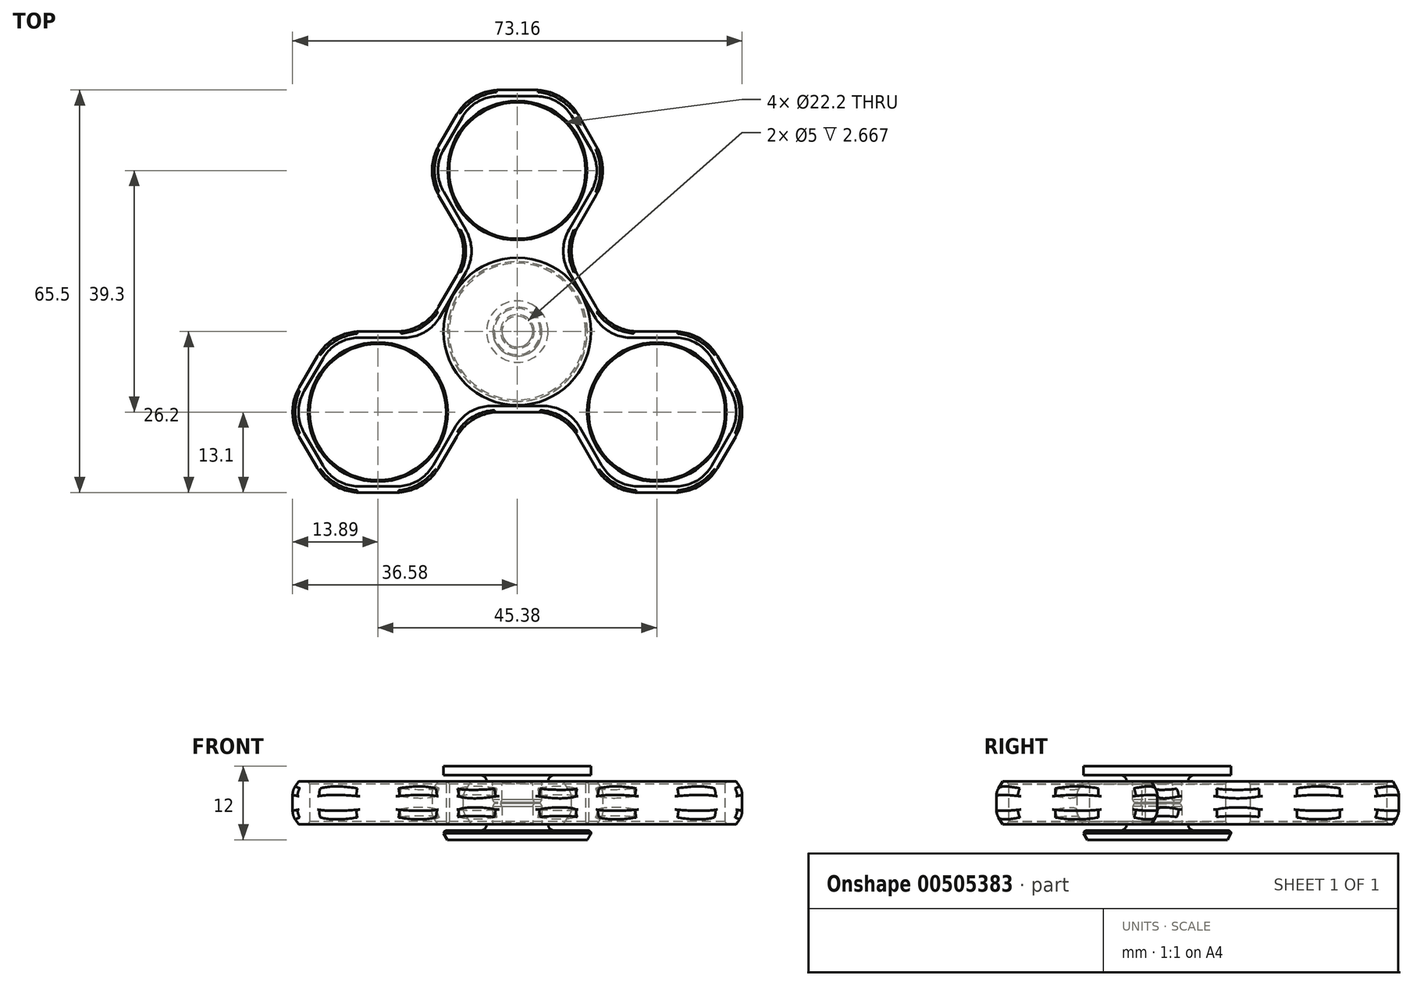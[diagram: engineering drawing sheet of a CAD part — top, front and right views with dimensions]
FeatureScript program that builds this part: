
annotation { "Feature Type Name" : "Feature", "Feature Type Description" : "" }
export const myFeature = defineFeature(function(context is Context, id is Id, definition is map)
    precondition{}
    {
        {
            var Q0;
            Q0=qCreatedBy(makeId("Top.planeOp"),FACE);
            var sketch = newSketch(context, id + "F0", { "sketchPlane" : qUnion([Q0])});
            skCircle(sketch, "E0.cCircle", {"center": v(0, 26.2) * mm, "radius": 13.1 * mm, "construction": true});
            skLineSegment(sketch, "E0.0", {"start": v(7.56, 13.1) * mm, "end": v(-7.56, 13.1) * mm});
            skLineSegment(sketch, "E0.1", {"start": v(-7.56, 13.1) * mm, "end": v(-15.13, 26.2) * mm});
            skLineSegment(sketch, "E0.2", {"start": v(-15.13, 26.2) * mm, "end": v(-7.56, 39.3) * mm});
            skLineSegment(sketch, "E0.3", {"start": v(-7.56, 39.3) * mm, "end": v(7.56, 39.3) * mm});
            skLineSegment(sketch, "E0.4", {"start": v(7.56, 39.3) * mm, "end": v(15.13, 26.2) * mm});
            skLineSegment(sketch, "E0.5", {"start": v(15.13, 26.2) * mm, "end": v(7.56, 13.1) * mm});
            skPoint(sketch, "E0.0.midPoint", {"position": v(0, 13.1) * mm});
            skCircle(sketch, "E1", {"center": v(0, 26.2) * mm, "radius": 11.1 * mm});
            skCircle(sketch, "E2.1.0", {"center": v(-22.69, -13.1) * mm, "radius": 11.1 * mm});
            skLineSegment(sketch, "E2.1.1", {"start": v(-30.25, -26.2) * mm, "end": v(-37.82, -13.1) * mm});
            skLineSegment(sketch, "E2.1.2", {"start": v(-37.82, -13.1) * mm, "end": v(-30.25, 0) * mm});
            skLineSegment(sketch, "E2.1.3", {"start": v(-30.25, 0) * mm, "end": v(-15.13, 0) * mm});
            skLineSegment(sketch, "E2.1.4", {"start": v(-15.13, 0) * mm, "end": v(-7.56, -13.1) * mm});
            skLineSegment(sketch, "E2.1.5", {"start": v(-7.56, -13.1) * mm, "end": v(-15.13, -26.2) * mm});
            skLineSegment(sketch, "E2.1.6", {"start": v(-15.13, -26.2) * mm, "end": v(-30.25, -26.2) * mm});
            skCircle(sketch, "E2.2.0", {"center": v(22.69, -13.1) * mm, "radius": 11.1 * mm});
            skLineSegment(sketch, "E2.2.1", {"start": v(37.82, -13.1) * mm, "end": v(30.25, -26.2) * mm});
            skLineSegment(sketch, "E2.2.2", {"start": v(30.25, -26.2) * mm, "end": v(15.13, -26.2) * mm});
            skLineSegment(sketch, "E2.2.3", {"start": v(15.13, -26.2) * mm, "end": v(7.56, -13.1) * mm});
            skLineSegment(sketch, "E2.2.4", {"start": v(7.56, -13.1) * mm, "end": v(15.13, 0) * mm});
            skLineSegment(sketch, "E2.2.5", {"start": v(15.13, 0) * mm, "end": v(30.25, 0) * mm});
            skLineSegment(sketch, "E2.2.6", {"start": v(30.25, 0) * mm, "end": v(37.82, -13.1) * mm});
            skPoint(sketch, "E2.center", {"position": v(0, 0) * mm});
            skCircle(sketch, "E3", {"center": v(0, 0) * mm, "radius": 11.1 * mm});
            skLineSegment(sketch, "E4", {"start": v(7.56, 13.1) * mm, "end": v(15.13, 0) * mm});
            skLineSegment(sketch, "E5", {"start": v(7.56, -13.1) * mm, "end": v(-7.56, -13.1) * mm});
            skLineSegment(sketch, "E6", {"start": v(-15.13, 0) * mm, "end": v(-7.56, 13.1) * mm});
            skCircle(sketch, "E7", {"center": v(0, 0) * mm, "radius": 40.02 * mm, "construction": true});
            skSolve(sketch);
        }
        {
            var Q0;
            Q0=makeQuery(id+"F0.imprint","IMPRINT",FACE,{"disambiguationData":[TD([[makeQuery(id+"F0.imprint","IMPRINT",EDGE,{"derivedFrom":sQuery(id+"F0.wireOp",EDGE,"E0.0")}),-1.0]])]});
            var Q1;
            Q1=makeQuery(id+"F0.imprint","IMPRINT",FACE,{"disambiguationData":[TD([[makeQuery(id+"F0.imprint","IMPRINT",EDGE,{"derivedFrom":sQuery(id+"F0.wireOp",EDGE,"E0.0")}),1.0]])]});
            var Q2;
            Q2=makeQuery(id+"F0.imprint","IMPRINT",FACE,{"disambiguationData":[TD([[makeQuery(id+"F0.imprint","IMPRINT",EDGE,{"derivedFrom":sQuery(id+"F0.wireOp",EDGE,"E2.1.0")}),-1.0]])]});
            var Q3;
            Q3=makeQuery(id+"F0.imprint","IMPRINT",FACE,{"disambiguationData":[TD([[makeQuery(id+"F0.imprint","IMPRINT",EDGE,{"derivedFrom":sQuery(id+"F0.wireOp",EDGE,"E2.2.0")}),-1.0]])]});
            extrude(context, id + "F1", {"entities" : qUnion([Q0, Q1, Q2, Q3]), "depth" : 7 * mm});
        }
        {
            var Q0;
            Q0=makeQuery(id+"F1.opExtrude","CAP_EDGE",EDGE,{"disambiguationData":[OSD([sQuery(id+"F0.wireOp",EDGE,"E0.3")])],"isStart":false});
            var Q1;
            Q1=makeQuery(id+"F1.opExtrude","CAP_EDGE",EDGE,{"disambiguationData":[OSD([sQuery(id+"F0.wireOp",EDGE,"E0.2")])],"isStart":false});
            var Q2;
            Q2=makeQuery(id+"F1.opExtrude","CAP_EDGE",EDGE,{"disambiguationData":[OSD([sQuery(id+"F0.wireOp",EDGE,"E0.1")])],"isStart":false});
            var Q3;
            Q3=makeQuery(id+"F1.opExtrude","CAP_EDGE",EDGE,{"disambiguationData":[OSD([sQuery(id+"F0.wireOp",EDGE,"E0.4")])],"isStart":false});
            var Q4;
            Q4=makeQuery(id+"F1.opExtrude","CAP_EDGE",EDGE,{"disambiguationData":[OSD([sQuery(id+"F0.wireOp",EDGE,"E0.5")])],"isStart":false});
            var Q5;
            Q5=makeQuery(id+"F1.opExtrude","CAP_EDGE",EDGE,{"disambiguationData":[OSD([sQuery(id+"F0.wireOp",EDGE,"E6")])],"isStart":false});
            var Q6;
            Q6=makeQuery(id+"F1.opExtrude","CAP_EDGE",EDGE,{"disambiguationData":[OSD([sQuery(id+"F0.wireOp",EDGE,"E4")])],"isStart":false});
            var Q7;
            Q7=makeQuery(id+"F1.opExtrude","CAP_EDGE",EDGE,{"disambiguationData":[OSD([sQuery(id+"F0.wireOp",EDGE,"E2.2.5")])],"isStart":false});
            var Q8;
            Q8=makeQuery(id+"F1.opExtrude","CAP_EDGE",EDGE,{"disambiguationData":[OSD([sQuery(id+"F0.wireOp",EDGE,"E2.2.6")])],"isStart":false});
            var Q9;
            Q9=makeQuery(id+"F1.opExtrude","CAP_EDGE",EDGE,{"disambiguationData":[OSD([sQuery(id+"F0.wireOp",EDGE,"E2.2.1")])],"isStart":false});
            var Q10;
            Q10=makeQuery(id+"F1.opExtrude","CAP_EDGE",EDGE,{"disambiguationData":[OSD([sQuery(id+"F0.wireOp",EDGE,"E2.2.2")])],"isStart":false});
            var Q11;
            Q11=makeQuery(id+"F1.opExtrude","CAP_EDGE",EDGE,{"disambiguationData":[OSD([sQuery(id+"F0.wireOp",EDGE,"E2.2.3")])],"isStart":false});
            var Q12;
            Q12=makeQuery(id+"F1.opExtrude","CAP_EDGE",EDGE,{"disambiguationData":[OSD([sQuery(id+"F0.wireOp",EDGE,"E5")])],"isStart":false});
            var Q13;
            Q13=makeQuery(id+"F1.opExtrude","CAP_EDGE",EDGE,{"disambiguationData":[OSD([sQuery(id+"F0.wireOp",EDGE,"E2.1.5")])],"isStart":false});
            var Q14;
            Q14=makeQuery(id+"F1.opExtrude","CAP_EDGE",EDGE,{"disambiguationData":[OSD([sQuery(id+"F0.wireOp",EDGE,"E2.1.6")])],"isStart":false});
            var Q15;
            Q15=makeQuery(id+"F1.opExtrude","CAP_EDGE",EDGE,{"disambiguationData":[OSD([sQuery(id+"F0.wireOp",EDGE,"E2.1.1")])],"isStart":false});
            var Q16;
            Q16=makeQuery(id+"F1.opExtrude","CAP_EDGE",EDGE,{"disambiguationData":[OSD([sQuery(id+"F0.wireOp",EDGE,"E2.1.2")])],"isStart":false});
            var Q17;
            Q17=makeQuery(id+"F1.opExtrude","CAP_EDGE",EDGE,{"disambiguationData":[OSD([sQuery(id+"F0.wireOp",EDGE,"E2.1.3")])],"isStart":false});
            chamfer(context, id + "F2", {"entities" : qUnion([Q0, Q1, Q2, Q3, Q4, Q5, Q6, Q7, Q8, Q9, Q10, Q11, Q12, Q13, Q14, Q15, Q16, Q17]), "chamferType" : ChamferType.OFFSET_ANGLE, "width" : 1 * mm, "oppositeDirection" : true, "angle" : 60 * degree, "tangentPropagation" : true});
        }
        {
            var Q0;
            Q0=makeQuery(id+"F1.opExtrude","CAP_EDGE",EDGE,{"disambiguationData":[OSD([sQuery(id+"F0.wireOp",EDGE,"E2.1.3")])],"isStart":true});
            var Q1;
            Q1=makeQuery(id+"F1.opExtrude","CAP_EDGE",EDGE,{"disambiguationData":[OSD([sQuery(id+"F0.wireOp",EDGE,"E2.1.2")])],"isStart":true});
            var Q2;
            Q2=makeQuery(id+"F1.opExtrude","CAP_EDGE",EDGE,{"disambiguationData":[OSD([sQuery(id+"F0.wireOp",EDGE,"E2.1.1")])],"isStart":true});
            var Q3;
            Q3=makeQuery(id+"F1.opExtrude","CAP_EDGE",EDGE,{"disambiguationData":[OSD([sQuery(id+"F0.wireOp",EDGE,"E2.1.6")])],"isStart":true});
            var Q4;
            Q4=makeQuery(id+"F1.opExtrude","CAP_EDGE",EDGE,{"disambiguationData":[OSD([sQuery(id+"F0.wireOp",EDGE,"E2.1.5")])],"isStart":true});
            var Q5;
            Q5=makeQuery(id+"F1.opExtrude","CAP_EDGE",EDGE,{"disambiguationData":[OSD([sQuery(id+"F0.wireOp",EDGE,"E5")])],"isStart":true});
            var Q6;
            Q6=makeQuery(id+"F1.opExtrude","CAP_EDGE",EDGE,{"disambiguationData":[OSD([sQuery(id+"F0.wireOp",EDGE,"E2.2.3")])],"isStart":true});
            var Q7;
            Q7=makeQuery(id+"F1.opExtrude","CAP_EDGE",EDGE,{"disambiguationData":[OSD([sQuery(id+"F0.wireOp",EDGE,"E2.2.2")])],"isStart":true});
            var Q8;
            Q8=makeQuery(id+"F1.opExtrude","CAP_EDGE",EDGE,{"disambiguationData":[OSD([sQuery(id+"F0.wireOp",EDGE,"E2.2.1")])],"isStart":true});
            var Q9;
            Q9=makeQuery(id+"F1.opExtrude","CAP_EDGE",EDGE,{"disambiguationData":[OSD([sQuery(id+"F0.wireOp",EDGE,"E2.2.6")])],"isStart":true});
            var Q10;
            Q10=makeQuery(id+"F1.opExtrude","CAP_EDGE",EDGE,{"disambiguationData":[OSD([sQuery(id+"F0.wireOp",EDGE,"E2.2.5")])],"isStart":true});
            var Q11;
            Q11=makeQuery(id+"F1.opExtrude","CAP_EDGE",EDGE,{"disambiguationData":[OSD([sQuery(id+"F0.wireOp",EDGE,"E4")])],"isStart":true});
            var Q12;
            Q12=makeQuery(id+"F1.opExtrude","CAP_EDGE",EDGE,{"disambiguationData":[OSD([sQuery(id+"F0.wireOp",EDGE,"E0.5")])],"isStart":true});
            var Q13;
            Q13=makeQuery(id+"F1.opExtrude","CAP_EDGE",EDGE,{"disambiguationData":[OSD([sQuery(id+"F0.wireOp",EDGE,"E6")])],"isStart":true});
            var Q14;
            Q14=makeQuery(id+"F1.opExtrude","CAP_EDGE",EDGE,{"disambiguationData":[OSD([sQuery(id+"F0.wireOp",EDGE,"E0.1")])],"isStart":true});
            var Q15;
            Q15=makeQuery(id+"F1.opExtrude","CAP_EDGE",EDGE,{"disambiguationData":[OSD([sQuery(id+"F0.wireOp",EDGE,"E0.2")])],"isStart":true});
            var Q16;
            Q16=makeQuery(id+"F1.opExtrude","CAP_EDGE",EDGE,{"disambiguationData":[OSD([sQuery(id+"F0.wireOp",EDGE,"E0.3")])],"isStart":true});
            var Q17;
            Q17=makeQuery(id+"F1.opExtrude","CAP_EDGE",EDGE,{"disambiguationData":[OSD([sQuery(id+"F0.wireOp",EDGE,"E0.4")])],"isStart":true});
            chamfer(context, id + "F3", {"entities" : qUnion([Q0, Q1, Q2, Q3, Q4, Q5, Q6, Q7, Q8, Q9, Q10, Q11, Q12, Q13, Q14, Q15, Q16, Q17]), "chamferType" : ChamferType.OFFSET_ANGLE, "width" : 1 * mm, "oppositeDirection" : false, "angle" : 60 * degree, "tangentPropagation" : true});
        }
        {
            var Q0;
            Q0=makeQuery(id+"F1.opExtrude","SWEPT_EDGE",EDGE,{"disambiguationData":[OSD([sQuery(id+"F0.wireOp",EDGE,"E0.1"),sQuery(id+"F0.wireOp",EDGE,"E0.2")])]});
            var Q1;
            Q1=makeQuery(id+"F3.opChamfer","BLEND_EDGE",EDGE,{"blendedFrom":[makeQuery(id+"F1.opExtrude","CAP_EDGE",EDGE,{"disambiguationData":[OSD([sQuery(id+"F0.wireOp",EDGE,"E0.1")])],"isStart":true}),makeQuery(id+"F1.opExtrude","CAP_EDGE",EDGE,{"disambiguationData":[OSD([sQuery(id+"F0.wireOp",EDGE,"E0.2")])],"isStart":true})],"blendedInto":[]});
            var Q2;
            Q2=makeQuery(id+"F2.opChamfer","BLEND_EDGE",EDGE,{"blendedFrom":[makeQuery(id+"F1.opExtrude","CAP_EDGE",EDGE,{"disambiguationData":[OSD([sQuery(id+"F0.wireOp",EDGE,"E0.1")])],"isStart":false}),makeQuery(id+"F1.opExtrude","CAP_EDGE",EDGE,{"disambiguationData":[OSD([sQuery(id+"F0.wireOp",EDGE,"E0.2")])],"isStart":false})],"blendedInto":[]});
            var Q3;
            Q3=makeQuery(id+"F1.opExtrude","SWEPT_EDGE",EDGE,{"disambiguationData":[OSD([sQuery(id+"F0.wireOp",EDGE,"E0.2"),sQuery(id+"F0.wireOp",EDGE,"E0.3")])]});
            var Q4;
            Q4=makeQuery(id+"F3.opChamfer","BLEND_EDGE",EDGE,{"blendedFrom":[makeQuery(id+"F1.opExtrude","CAP_EDGE",EDGE,{"disambiguationData":[OSD([sQuery(id+"F0.wireOp",EDGE,"E0.2")])],"isStart":true}),makeQuery(id+"F1.opExtrude","CAP_EDGE",EDGE,{"disambiguationData":[OSD([sQuery(id+"F0.wireOp",EDGE,"E0.3")])],"isStart":true})],"blendedInto":[]});
            var Q5;
            Q5=makeQuery(id+"F2.opChamfer","BLEND_EDGE",EDGE,{"blendedFrom":[makeQuery(id+"F1.opExtrude","CAP_EDGE",EDGE,{"disambiguationData":[OSD([sQuery(id+"F0.wireOp",EDGE,"E0.2")])],"isStart":false}),makeQuery(id+"F1.opExtrude","CAP_EDGE",EDGE,{"disambiguationData":[OSD([sQuery(id+"F0.wireOp",EDGE,"E0.3")])],"isStart":false})],"blendedInto":[]});
            var Q6;
            Q6=makeQuery(id+"F3.opChamfer","BLEND_EDGE",EDGE,{"blendedFrom":[makeQuery(id+"F1.opExtrude","CAP_EDGE",EDGE,{"disambiguationData":[OSD([sQuery(id+"F0.wireOp",EDGE,"E0.3")])],"isStart":true}),makeQuery(id+"F1.opExtrude","CAP_EDGE",EDGE,{"disambiguationData":[OSD([sQuery(id+"F0.wireOp",EDGE,"E0.4")])],"isStart":true})],"blendedInto":[]});
            var Q7;
            Q7=makeQuery(id+"F1.opExtrude","SWEPT_EDGE",EDGE,{"disambiguationData":[OSD([sQuery(id+"F0.wireOp",EDGE,"E0.3"),sQuery(id+"F0.wireOp",EDGE,"E0.4")])]});
            var Q8;
            Q8=makeQuery(id+"F2.opChamfer","BLEND_EDGE",EDGE,{"blendedFrom":[makeQuery(id+"F1.opExtrude","CAP_EDGE",EDGE,{"disambiguationData":[OSD([sQuery(id+"F0.wireOp",EDGE,"E0.3")])],"isStart":false}),makeQuery(id+"F1.opExtrude","CAP_EDGE",EDGE,{"disambiguationData":[OSD([sQuery(id+"F0.wireOp",EDGE,"E0.4")])],"isStart":false})],"blendedInto":[]});
            var Q9;
            Q9=makeQuery(id+"F3.opChamfer","BLEND_EDGE",EDGE,{"blendedFrom":[makeQuery(id+"F1.opExtrude","CAP_EDGE",EDGE,{"disambiguationData":[OSD([sQuery(id+"F0.wireOp",EDGE,"E0.4")])],"isStart":true}),makeQuery(id+"F1.opExtrude","CAP_EDGE",EDGE,{"disambiguationData":[OSD([sQuery(id+"F0.wireOp",EDGE,"E0.5")])],"isStart":true})],"blendedInto":[]});
            var Q10;
            Q10=makeQuery(id+"F1.opExtrude","SWEPT_EDGE",EDGE,{"disambiguationData":[OSD([sQuery(id+"F0.wireOp",EDGE,"E0.4"),sQuery(id+"F0.wireOp",EDGE,"E0.5")])]});
            var Q11;
            Q11=makeQuery(id+"F2.opChamfer","BLEND_EDGE",EDGE,{"blendedFrom":[makeQuery(id+"F1.opExtrude","CAP_EDGE",EDGE,{"disambiguationData":[OSD([sQuery(id+"F0.wireOp",EDGE,"E0.4")])],"isStart":false}),makeQuery(id+"F1.opExtrude","CAP_EDGE",EDGE,{"disambiguationData":[OSD([sQuery(id+"F0.wireOp",EDGE,"E0.5")])],"isStart":false})],"blendedInto":[]});
            var Q12;
            Q12=makeQuery(id+"F3.opChamfer","BLEND_EDGE",EDGE,{"blendedFrom":[makeQuery(id+"F1.opExtrude","CAP_EDGE",EDGE,{"disambiguationData":[OSD([sQuery(id+"F0.wireOp",EDGE,"E0.5")])],"isStart":true}),makeQuery(id+"F1.opExtrude","CAP_EDGE",EDGE,{"disambiguationData":[OSD([sQuery(id+"F0.wireOp",EDGE,"E4")])],"isStart":true})],"blendedInto":[]});
            var Q13;
            Q13=makeQuery(id+"F1.opExtrude","SWEPT_EDGE",EDGE,{"disambiguationData":[OSD([sQuery(id+"F0.wireOp",EDGE,"E0.0"),sQuery(id+"F0.wireOp",EDGE,"E0.5"),sQuery(id+"F0.wireOp",EDGE,"E4")])]});
            var Q14;
            Q14=makeQuery(id+"F2.opChamfer","BLEND_EDGE",EDGE,{"blendedFrom":[makeQuery(id+"F1.opExtrude","CAP_EDGE",EDGE,{"disambiguationData":[OSD([sQuery(id+"F0.wireOp",EDGE,"E0.5")])],"isStart":false}),makeQuery(id+"F1.opExtrude","CAP_EDGE",EDGE,{"disambiguationData":[OSD([sQuery(id+"F0.wireOp",EDGE,"E4")])],"isStart":false})],"blendedInto":[]});
            var Q15;
            Q15=makeQuery(id+"F3.opChamfer","BLEND_EDGE",EDGE,{"blendedFrom":[makeQuery(id+"F1.opExtrude","CAP_EDGE",EDGE,{"disambiguationData":[OSD([sQuery(id+"F0.wireOp",EDGE,"E2.2.5")])],"isStart":true}),makeQuery(id+"F1.opExtrude","CAP_EDGE",EDGE,{"disambiguationData":[OSD([sQuery(id+"F0.wireOp",EDGE,"E4")])],"isStart":true})],"blendedInto":[]});
            var Q16;
            Q16=makeQuery(id+"F1.opExtrude","SWEPT_EDGE",EDGE,{"disambiguationData":[OSD([sQuery(id+"F0.wireOp",EDGE,"E2.2.4"),sQuery(id+"F0.wireOp",EDGE,"E2.2.5"),sQuery(id+"F0.wireOp",EDGE,"E4")])]});
            var Q17;
            Q17=makeQuery(id+"F2.opChamfer","BLEND_EDGE",EDGE,{"blendedFrom":[makeQuery(id+"F1.opExtrude","CAP_EDGE",EDGE,{"disambiguationData":[OSD([sQuery(id+"F0.wireOp",EDGE,"E2.2.5")])],"isStart":false}),makeQuery(id+"F1.opExtrude","CAP_EDGE",EDGE,{"disambiguationData":[OSD([sQuery(id+"F0.wireOp",EDGE,"E4")])],"isStart":false})],"blendedInto":[]});
            var Q18;
            Q18=makeQuery(id+"F2.opChamfer","BLEND_EDGE",EDGE,{"blendedFrom":[makeQuery(id+"F1.opExtrude","CAP_EDGE",EDGE,{"disambiguationData":[OSD([sQuery(id+"F0.wireOp",EDGE,"E2.2.5")])],"isStart":false}),makeQuery(id+"F1.opExtrude","CAP_EDGE",EDGE,{"disambiguationData":[OSD([sQuery(id+"F0.wireOp",EDGE,"E2.2.6")])],"isStart":false})],"blendedInto":[]});
            var Q19;
            Q19=makeQuery(id+"F1.opExtrude","SWEPT_EDGE",EDGE,{"disambiguationData":[OSD([sQuery(id+"F0.wireOp",EDGE,"E2.2.5"),sQuery(id+"F0.wireOp",EDGE,"E2.2.6")])]});
            var Q20;
            Q20=makeQuery(id+"F3.opChamfer","BLEND_EDGE",EDGE,{"blendedFrom":[makeQuery(id+"F1.opExtrude","CAP_EDGE",EDGE,{"disambiguationData":[OSD([sQuery(id+"F0.wireOp",EDGE,"E2.2.5")])],"isStart":true}),makeQuery(id+"F1.opExtrude","CAP_EDGE",EDGE,{"disambiguationData":[OSD([sQuery(id+"F0.wireOp",EDGE,"E2.2.6")])],"isStart":true})],"blendedInto":[]});
            var Q21;
            Q21=makeQuery(id+"F3.opChamfer","BLEND_EDGE",EDGE,{"blendedFrom":[makeQuery(id+"F1.opExtrude","CAP_EDGE",EDGE,{"disambiguationData":[OSD([sQuery(id+"F0.wireOp",EDGE,"E2.2.1")])],"isStart":true}),makeQuery(id+"F1.opExtrude","CAP_EDGE",EDGE,{"disambiguationData":[OSD([sQuery(id+"F0.wireOp",EDGE,"E2.2.6")])],"isStart":true})],"blendedInto":[]});
            var Q22;
            Q22=makeQuery(id+"F1.opExtrude","SWEPT_EDGE",EDGE,{"disambiguationData":[OSD([sQuery(id+"F0.wireOp",EDGE,"E2.2.1"),sQuery(id+"F0.wireOp",EDGE,"E2.2.6")])]});
            var Q23;
            Q23=makeQuery(id+"F2.opChamfer","BLEND_EDGE",EDGE,{"blendedFrom":[makeQuery(id+"F1.opExtrude","CAP_EDGE",EDGE,{"disambiguationData":[OSD([sQuery(id+"F0.wireOp",EDGE,"E2.2.1")])],"isStart":false}),makeQuery(id+"F1.opExtrude","CAP_EDGE",EDGE,{"disambiguationData":[OSD([sQuery(id+"F0.wireOp",EDGE,"E2.2.6")])],"isStart":false})],"blendedInto":[]});
            var Q24;
            Q24=makeQuery(id+"F3.opChamfer","BLEND_EDGE",EDGE,{"blendedFrom":[makeQuery(id+"F1.opExtrude","CAP_EDGE",EDGE,{"disambiguationData":[OSD([sQuery(id+"F0.wireOp",EDGE,"E2.2.1")])],"isStart":true}),makeQuery(id+"F1.opExtrude","CAP_EDGE",EDGE,{"disambiguationData":[OSD([sQuery(id+"F0.wireOp",EDGE,"E2.2.2")])],"isStart":true})],"blendedInto":[]});
            var Q25;
            Q25=makeQuery(id+"F1.opExtrude","SWEPT_EDGE",EDGE,{"disambiguationData":[OSD([sQuery(id+"F0.wireOp",EDGE,"E2.2.1"),sQuery(id+"F0.wireOp",EDGE,"E2.2.2")])]});
            var Q26;
            Q26=makeQuery(id+"F2.opChamfer","BLEND_EDGE",EDGE,{"blendedFrom":[makeQuery(id+"F1.opExtrude","CAP_EDGE",EDGE,{"disambiguationData":[OSD([sQuery(id+"F0.wireOp",EDGE,"E2.2.1")])],"isStart":false}),makeQuery(id+"F1.opExtrude","CAP_EDGE",EDGE,{"disambiguationData":[OSD([sQuery(id+"F0.wireOp",EDGE,"E2.2.2")])],"isStart":false})],"blendedInto":[]});
            var Q27;
            Q27=makeQuery(id+"F3.opChamfer","BLEND_EDGE",EDGE,{"blendedFrom":[makeQuery(id+"F1.opExtrude","CAP_EDGE",EDGE,{"disambiguationData":[OSD([sQuery(id+"F0.wireOp",EDGE,"E2.2.2")])],"isStart":true}),makeQuery(id+"F1.opExtrude","CAP_EDGE",EDGE,{"disambiguationData":[OSD([sQuery(id+"F0.wireOp",EDGE,"E2.2.3")])],"isStart":true})],"blendedInto":[]});
            var Q28;
            Q28=makeQuery(id+"F1.opExtrude","SWEPT_EDGE",EDGE,{"disambiguationData":[OSD([sQuery(id+"F0.wireOp",EDGE,"E2.2.2"),sQuery(id+"F0.wireOp",EDGE,"E2.2.3")])]});
            var Q29;
            Q29=makeQuery(id+"F2.opChamfer","BLEND_EDGE",EDGE,{"blendedFrom":[makeQuery(id+"F1.opExtrude","CAP_EDGE",EDGE,{"disambiguationData":[OSD([sQuery(id+"F0.wireOp",EDGE,"E2.2.2")])],"isStart":false}),makeQuery(id+"F1.opExtrude","CAP_EDGE",EDGE,{"disambiguationData":[OSD([sQuery(id+"F0.wireOp",EDGE,"E2.2.3")])],"isStart":false})],"blendedInto":[]});
            var Q30;
            Q30=makeQuery(id+"F3.opChamfer","BLEND_EDGE",EDGE,{"blendedFrom":[makeQuery(id+"F1.opExtrude","CAP_EDGE",EDGE,{"disambiguationData":[OSD([sQuery(id+"F0.wireOp",EDGE,"E2.2.3")])],"isStart":true}),makeQuery(id+"F1.opExtrude","CAP_EDGE",EDGE,{"disambiguationData":[OSD([sQuery(id+"F0.wireOp",EDGE,"E5")])],"isStart":true})],"blendedInto":[]});
            var Q31;
            Q31=makeQuery(id+"F1.opExtrude","SWEPT_EDGE",EDGE,{"disambiguationData":[OSD([sQuery(id+"F0.wireOp",EDGE,"E2.2.3"),sQuery(id+"F0.wireOp",EDGE,"E2.2.4"),sQuery(id+"F0.wireOp",EDGE,"E5")])]});
            var Q32;
            Q32=makeQuery(id+"F2.opChamfer","BLEND_EDGE",EDGE,{"blendedFrom":[makeQuery(id+"F1.opExtrude","CAP_EDGE",EDGE,{"disambiguationData":[OSD([sQuery(id+"F0.wireOp",EDGE,"E2.2.3")])],"isStart":false}),makeQuery(id+"F1.opExtrude","CAP_EDGE",EDGE,{"disambiguationData":[OSD([sQuery(id+"F0.wireOp",EDGE,"E5")])],"isStart":false})],"blendedInto":[]});
            var Q33;
            Q33=makeQuery(id+"F3.opChamfer","BLEND_EDGE",EDGE,{"blendedFrom":[makeQuery(id+"F1.opExtrude","CAP_EDGE",EDGE,{"disambiguationData":[OSD([sQuery(id+"F0.wireOp",EDGE,"E2.1.5")])],"isStart":true}),makeQuery(id+"F1.opExtrude","CAP_EDGE",EDGE,{"disambiguationData":[OSD([sQuery(id+"F0.wireOp",EDGE,"E5")])],"isStart":true})],"blendedInto":[]});
            var Q34;
            Q34=makeQuery(id+"F1.opExtrude","SWEPT_EDGE",EDGE,{"disambiguationData":[OSD([sQuery(id+"F0.wireOp",EDGE,"E2.1.4"),sQuery(id+"F0.wireOp",EDGE,"E2.1.5"),sQuery(id+"F0.wireOp",EDGE,"E5")])]});
            var Q35;
            Q35=makeQuery(id+"F2.opChamfer","BLEND_EDGE",EDGE,{"blendedFrom":[makeQuery(id+"F1.opExtrude","CAP_EDGE",EDGE,{"disambiguationData":[OSD([sQuery(id+"F0.wireOp",EDGE,"E2.1.5")])],"isStart":false}),makeQuery(id+"F1.opExtrude","CAP_EDGE",EDGE,{"disambiguationData":[OSD([sQuery(id+"F0.wireOp",EDGE,"E5")])],"isStart":false})],"blendedInto":[]});
            var Q36;
            Q36=makeQuery(id+"F3.opChamfer","BLEND_EDGE",EDGE,{"blendedFrom":[makeQuery(id+"F1.opExtrude","CAP_EDGE",EDGE,{"disambiguationData":[OSD([sQuery(id+"F0.wireOp",EDGE,"E2.1.5")])],"isStart":true}),makeQuery(id+"F1.opExtrude","CAP_EDGE",EDGE,{"disambiguationData":[OSD([sQuery(id+"F0.wireOp",EDGE,"E2.1.6")])],"isStart":true})],"blendedInto":[]});
            var Q37;
            Q37=makeQuery(id+"F1.opExtrude","SWEPT_EDGE",EDGE,{"disambiguationData":[OSD([sQuery(id+"F0.wireOp",EDGE,"E2.1.5"),sQuery(id+"F0.wireOp",EDGE,"E2.1.6")])]});
            var Q38;
            Q38=makeQuery(id+"F2.opChamfer","BLEND_EDGE",EDGE,{"blendedFrom":[makeQuery(id+"F1.opExtrude","CAP_EDGE",EDGE,{"disambiguationData":[OSD([sQuery(id+"F0.wireOp",EDGE,"E2.1.5")])],"isStart":false}),makeQuery(id+"F1.opExtrude","CAP_EDGE",EDGE,{"disambiguationData":[OSD([sQuery(id+"F0.wireOp",EDGE,"E2.1.6")])],"isStart":false})],"blendedInto":[]});
            var Q39;
            Q39=makeQuery(id+"F3.opChamfer","BLEND_EDGE",EDGE,{"blendedFrom":[makeQuery(id+"F1.opExtrude","CAP_EDGE",EDGE,{"disambiguationData":[OSD([sQuery(id+"F0.wireOp",EDGE,"E2.1.1")])],"isStart":true}),makeQuery(id+"F1.opExtrude","CAP_EDGE",EDGE,{"disambiguationData":[OSD([sQuery(id+"F0.wireOp",EDGE,"E2.1.6")])],"isStart":true})],"blendedInto":[]});
            var Q40;
            Q40=makeQuery(id+"F1.opExtrude","SWEPT_EDGE",EDGE,{"disambiguationData":[OSD([sQuery(id+"F0.wireOp",EDGE,"E2.1.1"),sQuery(id+"F0.wireOp",EDGE,"E2.1.6")])]});
            var Q41;
            Q41=makeQuery(id+"F2.opChamfer","BLEND_EDGE",EDGE,{"blendedFrom":[makeQuery(id+"F1.opExtrude","CAP_EDGE",EDGE,{"disambiguationData":[OSD([sQuery(id+"F0.wireOp",EDGE,"E2.1.1")])],"isStart":false}),makeQuery(id+"F1.opExtrude","CAP_EDGE",EDGE,{"disambiguationData":[OSD([sQuery(id+"F0.wireOp",EDGE,"E2.1.6")])],"isStart":false})],"blendedInto":[]});
            var Q42;
            Q42=makeQuery(id+"F3.opChamfer","BLEND_EDGE",EDGE,{"blendedFrom":[makeQuery(id+"F1.opExtrude","CAP_EDGE",EDGE,{"disambiguationData":[OSD([sQuery(id+"F0.wireOp",EDGE,"E2.1.1")])],"isStart":true}),makeQuery(id+"F1.opExtrude","CAP_EDGE",EDGE,{"disambiguationData":[OSD([sQuery(id+"F0.wireOp",EDGE,"E2.1.2")])],"isStart":true})],"blendedInto":[]});
            var Q43;
            Q43=makeQuery(id+"F1.opExtrude","SWEPT_EDGE",EDGE,{"disambiguationData":[OSD([sQuery(id+"F0.wireOp",EDGE,"E2.1.1"),sQuery(id+"F0.wireOp",EDGE,"E2.1.2")])]});
            var Q44;
            Q44=makeQuery(id+"F2.opChamfer","BLEND_EDGE",EDGE,{"blendedFrom":[makeQuery(id+"F1.opExtrude","CAP_EDGE",EDGE,{"disambiguationData":[OSD([sQuery(id+"F0.wireOp",EDGE,"E2.1.1")])],"isStart":false}),makeQuery(id+"F1.opExtrude","CAP_EDGE",EDGE,{"disambiguationData":[OSD([sQuery(id+"F0.wireOp",EDGE,"E2.1.2")])],"isStart":false})],"blendedInto":[]});
            var Q45;
            Q45=makeQuery(id+"F3.opChamfer","BLEND_EDGE",EDGE,{"blendedFrom":[makeQuery(id+"F1.opExtrude","CAP_EDGE",EDGE,{"disambiguationData":[OSD([sQuery(id+"F0.wireOp",EDGE,"E2.1.2")])],"isStart":true}),makeQuery(id+"F1.opExtrude","CAP_EDGE",EDGE,{"disambiguationData":[OSD([sQuery(id+"F0.wireOp",EDGE,"E2.1.3")])],"isStart":true})],"blendedInto":[]});
            var Q46;
            Q46=makeQuery(id+"F1.opExtrude","SWEPT_EDGE",EDGE,{"disambiguationData":[OSD([sQuery(id+"F0.wireOp",EDGE,"E2.1.2"),sQuery(id+"F0.wireOp",EDGE,"E2.1.3")])]});
            var Q47;
            Q47=makeQuery(id+"F2.opChamfer","BLEND_EDGE",EDGE,{"blendedFrom":[makeQuery(id+"F1.opExtrude","CAP_EDGE",EDGE,{"disambiguationData":[OSD([sQuery(id+"F0.wireOp",EDGE,"E2.1.2")])],"isStart":false}),makeQuery(id+"F1.opExtrude","CAP_EDGE",EDGE,{"disambiguationData":[OSD([sQuery(id+"F0.wireOp",EDGE,"E2.1.3")])],"isStart":false})],"blendedInto":[]});
            var Q48;
            Q48=makeQuery(id+"F3.opChamfer","BLEND_EDGE",EDGE,{"blendedFrom":[makeQuery(id+"F1.opExtrude","CAP_EDGE",EDGE,{"disambiguationData":[OSD([sQuery(id+"F0.wireOp",EDGE,"E2.1.3")])],"isStart":true}),makeQuery(id+"F1.opExtrude","CAP_EDGE",EDGE,{"disambiguationData":[OSD([sQuery(id+"F0.wireOp",EDGE,"E6")])],"isStart":true})],"blendedInto":[]});
            var Q49;
            Q49=makeQuery(id+"F1.opExtrude","SWEPT_EDGE",EDGE,{"disambiguationData":[OSD([sQuery(id+"F0.wireOp",EDGE,"E2.1.3"),sQuery(id+"F0.wireOp",EDGE,"E2.1.4"),sQuery(id+"F0.wireOp",EDGE,"E6")])]});
            var Q50;
            Q50=makeQuery(id+"F2.opChamfer","BLEND_EDGE",EDGE,{"blendedFrom":[makeQuery(id+"F1.opExtrude","CAP_EDGE",EDGE,{"disambiguationData":[OSD([sQuery(id+"F0.wireOp",EDGE,"E2.1.3")])],"isStart":false}),makeQuery(id+"F1.opExtrude","CAP_EDGE",EDGE,{"disambiguationData":[OSD([sQuery(id+"F0.wireOp",EDGE,"E6")])],"isStart":false})],"blendedInto":[]});
            var Q51;
            Q51=makeQuery(id+"F3.opChamfer","BLEND_EDGE",EDGE,{"blendedFrom":[makeQuery(id+"F1.opExtrude","CAP_EDGE",EDGE,{"disambiguationData":[OSD([sQuery(id+"F0.wireOp",EDGE,"E0.1")])],"isStart":true}),makeQuery(id+"F1.opExtrude","CAP_EDGE",EDGE,{"disambiguationData":[OSD([sQuery(id+"F0.wireOp",EDGE,"E6")])],"isStart":true})],"blendedInto":[]});
            var Q52;
            Q52=makeQuery(id+"F1.opExtrude","SWEPT_EDGE",EDGE,{"disambiguationData":[OSD([sQuery(id+"F0.wireOp",EDGE,"E0.0"),sQuery(id+"F0.wireOp",EDGE,"E0.1"),sQuery(id+"F0.wireOp",EDGE,"E6")])]});
            var Q53;
            Q53=makeQuery(id+"F2.opChamfer","BLEND_EDGE",EDGE,{"blendedFrom":[makeQuery(id+"F1.opExtrude","CAP_EDGE",EDGE,{"disambiguationData":[OSD([sQuery(id+"F0.wireOp",EDGE,"E0.1")])],"isStart":false}),makeQuery(id+"F1.opExtrude","CAP_EDGE",EDGE,{"disambiguationData":[OSD([sQuery(id+"F0.wireOp",EDGE,"E6")])],"isStart":false})],"blendedInto":[]});
            fillet(context, id + "F4", {"entities" : qUnion([Q0, Q1, Q2, Q3, Q4, Q5, Q6, Q7, Q8, Q9, Q10, Q11, Q12, Q13, Q14, Q15, Q16, Q17, Q18, Q19, Q20, Q21, Q22, Q23, Q24, Q25, Q26, Q27, Q28, Q29, Q30, Q31, Q32, Q33, Q34, Q35, Q36, Q37, Q38, Q39, Q40, Q41, Q42, Q43, Q44, Q45, Q46, Q47, Q48, Q49, Q50, Q51, Q52, Q53]), "radius" : 8 * mm, "tangentPropagation" : true, "allowEdgeOverflow" : false});
        }
        {
            var Q0;
            Q0=makeQuery(id+"F1.opExtrude","CAP_EDGE",EDGE,{"disambiguationData":[OSD([sQuery(id+"F0.wireOp",EDGE,"E2.2.0")])],"isStart":true});
            var Q1;
            Q1=makeQuery(id+"F1.opExtrude","CAP_EDGE",EDGE,{"disambiguationData":[OSD([sQuery(id+"F0.wireOp",EDGE,"E3")])],"isStart":true});
            var Q2;
            Q2=makeQuery(id+"F1.opExtrude","CAP_EDGE",EDGE,{"disambiguationData":[OSD([sQuery(id+"F0.wireOp",EDGE,"E2.1.0")])],"isStart":true});
            var Q3;
            Q3=makeQuery(id+"F1.opExtrude","CAP_EDGE",EDGE,{"disambiguationData":[OSD([sQuery(id+"F0.wireOp",EDGE,"E1")])],"isStart":true});
            chamfer(context, id + "F5", {"entities" : qUnion([Q0, Q1, Q2, Q3]), "chamferType" : ChamferType.OFFSET_ANGLE, "width" : 0.25 * mm, "oppositeDirection" : false, "angle" : 60 * degree, "tangentPropagation" : true});
        }
        {
            var Q0;
            Q0=makeQuery(id+"F1.opExtrude","CAP_EDGE",EDGE,{"disambiguationData":[OSD([sQuery(id+"F0.wireOp",EDGE,"E2.2.0")])],"isStart":false});
            var Q1;
            Q1=makeQuery(id+"F1.opExtrude","CAP_EDGE",EDGE,{"disambiguationData":[OSD([sQuery(id+"F0.wireOp",EDGE,"E3")])],"isStart":false});
            var Q2;
            Q2=makeQuery(id+"F1.opExtrude","CAP_EDGE",EDGE,{"disambiguationData":[OSD([sQuery(id+"F0.wireOp",EDGE,"E1")])],"isStart":false});
            var Q3;
            Q3=makeQuery(id+"F1.opExtrude","CAP_EDGE",EDGE,{"disambiguationData":[OSD([sQuery(id+"F0.wireOp",EDGE,"E2.1.0")])],"isStart":false});
            chamfer(context, id + "F6", {"entities" : qUnion([Q0, Q1, Q2, Q3]), "chamferType" : ChamferType.OFFSET_ANGLE, "width" : 0.25 * mm, "oppositeDirection" : true, "angle" : 60 * degree, "tangentPropagation" : true});
        }
        {
            var Q0;
            {var subQ0=sQuery(id+"F0.wireOp",EDGE,"E5");Q0=makeQuery(id+"F3.opChamfer","BLEND_EDGE",EDGE,{"blendedFrom":[makeQuery(id+"F1.opExtrude","CAP_EDGE",EDGE,{"disambiguationData":[OSD([subQ0])],"isStart":true}),makeQuery(id+"F1.opExtrude","SWEPT_FACE",FACE,{"disambiguationData":[OSD([subQ0])]})],"blendedInto":[makeQuery(id+"F1.opExtrude","SWEPT_FACE",FACE,{"disambiguationData":[OSD([subQ0])]})]});}
            var Q1;
            {var subQ0=sQuery(id+"F0.wireOp",EDGE,"E5");Q1=makeQuery(id+"F2.opChamfer","BLEND_EDGE",EDGE,{"blendedFrom":[makeQuery(id+"F1.opExtrude","CAP_EDGE",EDGE,{"disambiguationData":[OSD([subQ0])],"isStart":false}),makeQuery(id+"F1.opExtrude","SWEPT_FACE",FACE,{"disambiguationData":[OSD([subQ0])]})],"blendedInto":[makeQuery(id+"F1.opExtrude","SWEPT_FACE",FACE,{"disambiguationData":[OSD([subQ0])]})]});}
            fillet(context, id + "F7", {"entities" : qUnion([Q0, Q1]), "radius" : 2.5 * mm, "tangentPropagation" : true, "allowEdgeOverflow" : false});
        }
        {
            var Q0;
            Q0=qCreatedBy(makeId("Right.planeOp"),FACE);
            var sketch = newSketch(context, id + "F8", { "sketchPlane" : qUnion([Q0])});
            skLineSegment(sketch, "E8", {"start": v(0, -69.54) * mm, "end": v(0, 40.92) * mm});
            skLineSegment(sketch, "E9", {"start": v(-83.04, 0) * mm, "end": v(57, 0) * mm, "construction": true});
            skLineSegment(sketch, "E10", {"start": v(4, 3.4) * mm, "end": v(4, 0) * mm});
            skLineSegment(sketch, "E11", {"start": v(4, 0) * mm, "end": v(5, 0) * mm});
            skLineSegment(sketch, "E12", {"start": v(5, 0) * mm, "end": v(5, 0) * mm});
            skLineSegment(sketch, "E13", {"start": v(6, -1) * mm, "end": v(12, -1) * mm, "construction": true});
            skLineSegment(sketch, "E14", {"start": v(12, -1) * mm, "end": v(12, -2.5) * mm});
            skLineSegment(sketch, "E15", {"start": v(12, -2.5) * mm, "end": v(0, -2.5) * mm});
            skArc(sketch, "E16", {"start": v(8, -2.5) * mm, "mid": v(4.03, -1.75) * mm, "end": v(0, -1.5) * mm, "construction": true});
            skLineSegment(sketch, "E17", {"start": v(4, 3.4) * mm, "end": v(0, 3.4) * mm});
            skLineSegment(sketch, "E18", {"start": v(2.5, 3.4) * mm, "end": v(2.5, 0.3) * mm});
            skLineSegment(sketch, "E19", {"start": v(2.5, 0.3) * mm, "end": v(0, 0.3) * mm});
            skLineSegment(sketch, "E20", {"start": v(12, -1) * mm, "end": v(6, -1) * mm});
            skPoint(sketch, "E21.visualSharp", {"position": v(5, -1) * mm});
            skArc(sketch, "E21.filletArc", {"start": v(5, 0) * mm, "mid": v(5.3, -0.7) * mm, "end": v(6, -1) * mm});
            skSolve(sketch);
        }
        {
            var Q0;
            Q0=makeQuery(id+"F8.imprint","IMPRINT",FACE,{"disambiguationData":[TD([[makeQuery(id+"F8.imprint","IMPRINT",EDGE,{"derivedFrom":sQuery(id+"F8.wireOp",EDGE,"E10")}),-1.0]])]});
            var Q1;
            Q1=sQuery(id+"F8.wireOp",EDGE,"E8");
            revolve(context, id + "F9", {"entities" : qUnion([Q0]), "axis" : qUnion([Q1]), "revolveType" : RevolveType.FULL});
        }
        {
            var Q0;
            Q0=makeQuery(id+"F9.opRevolve","SWEPT_EDGE",EDGE,{"disambiguationData":[OSD([sQuery(id+"F8.wireOp",EDGE,"E10"),sQuery(id+"F8.wireOp",EDGE,"E17")])]});
            var Q1;
            Q1=makeQuery(id+"F9.opRevolve","SWEPT_EDGE",EDGE,{"disambiguationData":[OSD([sQuery(id+"F8.wireOp",EDGE,"E17"),sQuery(id+"F8.wireOp",EDGE,"E18")])]});
            chamfer(context, id + "F10", {"entities" : qUnion([Q0, Q1]), "chamferType" : ChamferType.OFFSET_ANGLE, "width" : 0.25 * mm, "oppositeDirection" : true, "angle" : 60 * degree, "tangentPropagation" : true});
        }
        {
            var Q0;
            Q0=qCreatedBy(makeId("Top.planeOp"),FACE);
            cPlane(context, id + "F11", {"entities" : qUnion([Q0]), "cplaneType" : CPlaneType.OFFSET, "offset" : (7 / 2) * mm, "width" : 150 * mm, "height" : 150 * mm});
        }
        {
            var Q0;
            Q0=makeQuery(id+"F9.opRevolve","SWEPT_BODY",BODY,{"disambiguationData":[OSD([sQuery(id+"F8.wireOp",EDGE,"E8"),sQuery(id+"F8.wireOp",EDGE,"E10"),sQuery(id+"F8.wireOp",EDGE,"E11"),sQuery(id+"F8.wireOp",EDGE,"E14"),sQuery(id+"F8.wireOp",EDGE,"SDO5igl3-3F4R-1kP7-bGDO-e8q0KM1T7T6S"),sQuery(id+"F8.wireOp",EDGE,"E15"),sQuery(id+"F8.wireOp",EDGE,"E16"),sQuery(id+"F8.wireOp",EDGE,"E17"),sQuery(id+"F8.wireOp",EDGE,"E18"),sQuery(id+"F8.wireOp",EDGE,"E19")])]});
            var Q1;
            Q1=qCreatedBy(id+"F11.planeOp",FACE);
            mirror(context, id + "F12", {"entities" : qUnion([Q0]), "mirrorPlane" : qUnion([Q1])});
        }
        {
            var Q0;
            Q0=makeQuery(id+"F9.opRevolve","SWEPT_EDGE",EDGE,{"disambiguationData":[OSD([sQuery(id+"F8.wireOp",EDGE,"E14"),sQuery(id+"F8.wireOp",EDGE,"E15")])]});
            chamfer(context, id + "F13", {"entities" : qUnion([Q0]), "chamferType" : ChamferType.OFFSET_ANGLE, "width" : 0.6 * mm, "oppositeDirection" : false, "angle" : 60 * degree, "tangentPropagation" : true});
        }
        {
            var Q0;
            Q0=makeQuery(id+"F9.opRevolve","SWEPT_EDGE",EDGE,{"disambiguationData":[OSD([sQuery(id+"F8.wireOp",EDGE,"nGK3Jv2O-nwwX-tW8B-eS2A-hI1keYIUavCy"),sQuery(id+"F8.wireOp",EDGE,"E20")])]});
            var Q1;
            Q1=makeQuery(id+"F9.opRevolve","SWEPT_EDGE",EDGE,{"disambiguationData":[OSD([sQuery(id+"F8.wireOp",EDGE,"93K0JSfv-FhNU-TQHY-CV6g-L6fCOftoNlT6"),sQuery(id+"F8.wireOp",EDGE,"nGK3Jv2O-nwwX-tW8B-eS2A-hI1keYIUavCy")])]});
            var Q2;
            Q2=makeQuery(id+"F9.opRevolve","SWEPT_EDGE",EDGE,{"disambiguationData":[OSD([sQuery(id+"F8.wireOp",EDGE,"E14"),sQuery(id+"F8.wireOp",EDGE,"93K0JSfv-FhNU-TQHY-CV6g-L6fCOftoNlT6")])]});
            fillet(context, id + "F14", {"entities" : qUnion([Q0, Q1, Q2]), "radius" : 0.5 * mm, "tangentPropagation" : true, "allowEdgeOverflow" : false});
        }
    });
